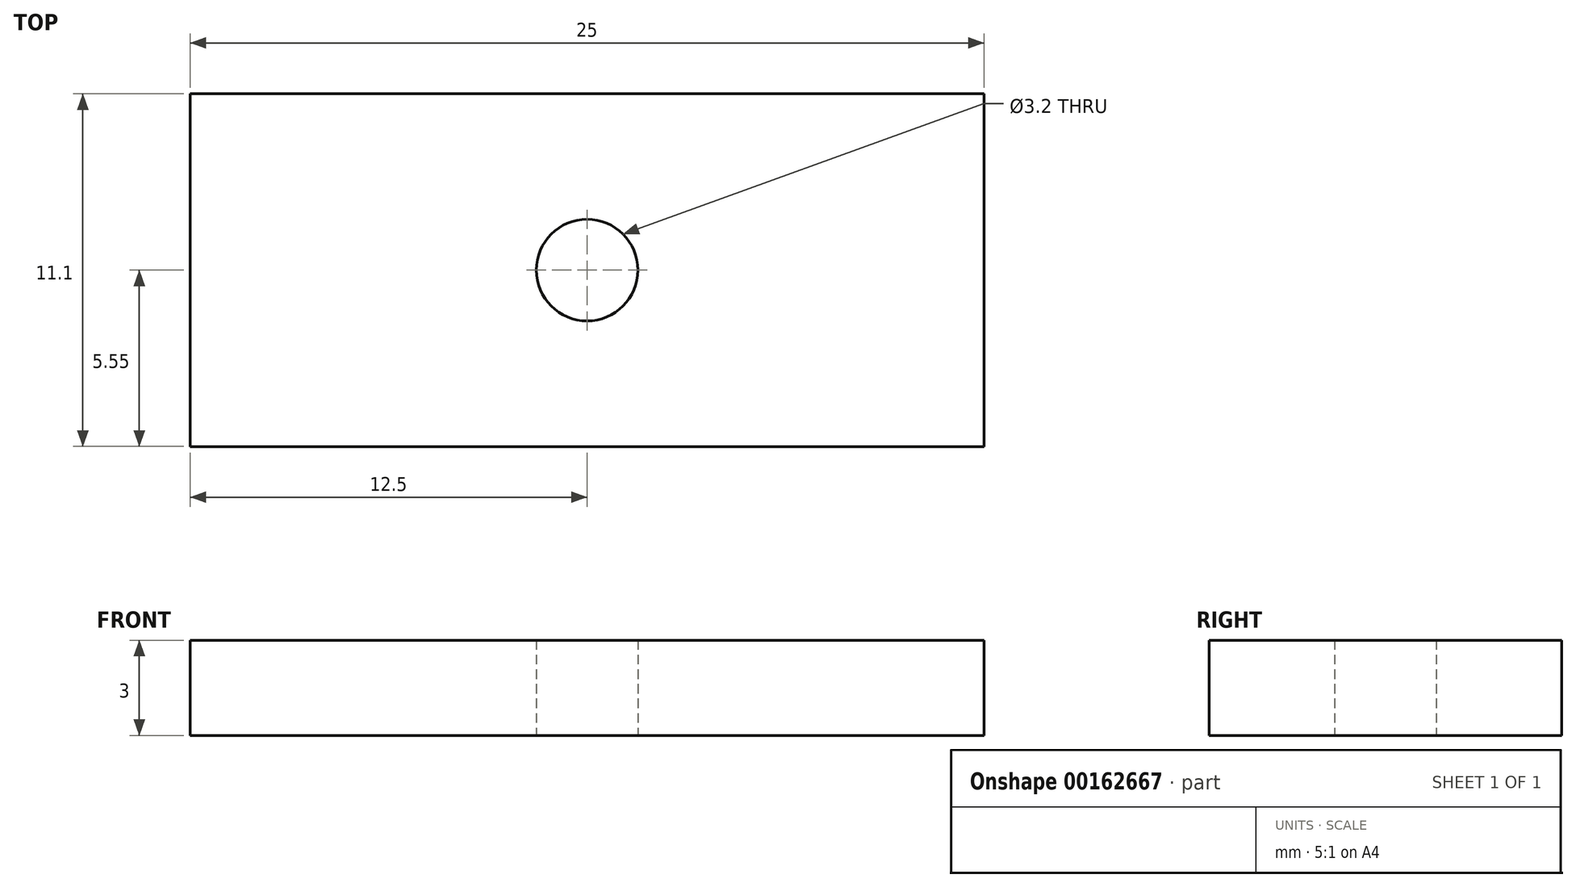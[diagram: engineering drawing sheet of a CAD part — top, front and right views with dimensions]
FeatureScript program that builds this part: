
annotation { "Feature Type Name" : "Feature", "Feature Type Description" : "" }
export const myFeature = defineFeature(function(context is Context, id is Id, definition is map)
    precondition{}
    {
        {
            var Q0;
            Q0=qCreatedBy(makeId("Top.planeOp"),FACE);
            var sketch = newSketch(context, id + "F0", { "sketchPlane" : qUnion([Q0])});
            skLineSegment(sketch, "E0.bottom", {"start": v(-12.5, 5.56) * mm, "end": v(12.5, 5.56) * mm});
            skLineSegment(sketch, "E0.top", {"start": v(-12.5, -5.55) * mm, "end": v(12.5, -5.55) * mm});
            skLineSegment(sketch, "E0.left", {"start": v(-12.5, 5.56) * mm, "end": v(-12.5, -5.55) * mm});
            skLineSegment(sketch, "E0.right", {"start": v(12.5, 5.56) * mm, "end": v(12.5, -5.55) * mm});
            skPoint(sketch, "E0.middle", {"position": v(0, 0) * mm});
            skCircle(sketch, "E1", {"center": v(0, 0) * mm, "radius": 1.6 * mm});
            skSolve(sketch);
        }
        {
            var Q0;
            Q0=makeQuery(id+"F0.imprint","IMPRINT",FACE,{"disambiguationData":[TD([[makeQuery(id+"F0.imprint","IMPRINT",EDGE,{"derivedFrom":sQuery(id+"F0.wireOp",EDGE,"E0.bottom")}),-1.0]])]});
            var Q1;
            Q1=makeQuery(id+"F0.imprint","IMPRINT",FACE,{"disambiguationData":[TD([[makeQuery(id+"F0.imprint","IMPRINT",EDGE,{"derivedFrom":sQuery(id+"F0.wireOp",EDGE,"E1")}),1.0]])]});
            extrude(context, id + "F1", {"entities" : qUnion([Q0, Q1]), "depth" : 3 * mm, "offsetDistance" : 25 * mm});
        }
        {
            var Q0;
            Q0=makeQuery(id+"F0.imprint","IMPRINT",FACE,{"disambiguationData":[TD([[makeQuery(id+"F0.imprint","IMPRINT",EDGE,{"derivedFrom":sQuery(id+"F0.wireOp",EDGE,"E1")}),1.0]])]});
            var Q1;
            Q1=sQuery(id+"F0.wireOp",EDGE,"E1");
            extrude(context, id + "F2", {"entities" : qUnion([Q0]), "operationType" : NewBodyOperationType.REMOVE, "surfaceEntities" : qUnion([Q1]), "endBound" : BoundingType.THROUGH_ALL, "depth" : 25 * mm, "offsetDistance" : 25 * mm});
        }
    });
